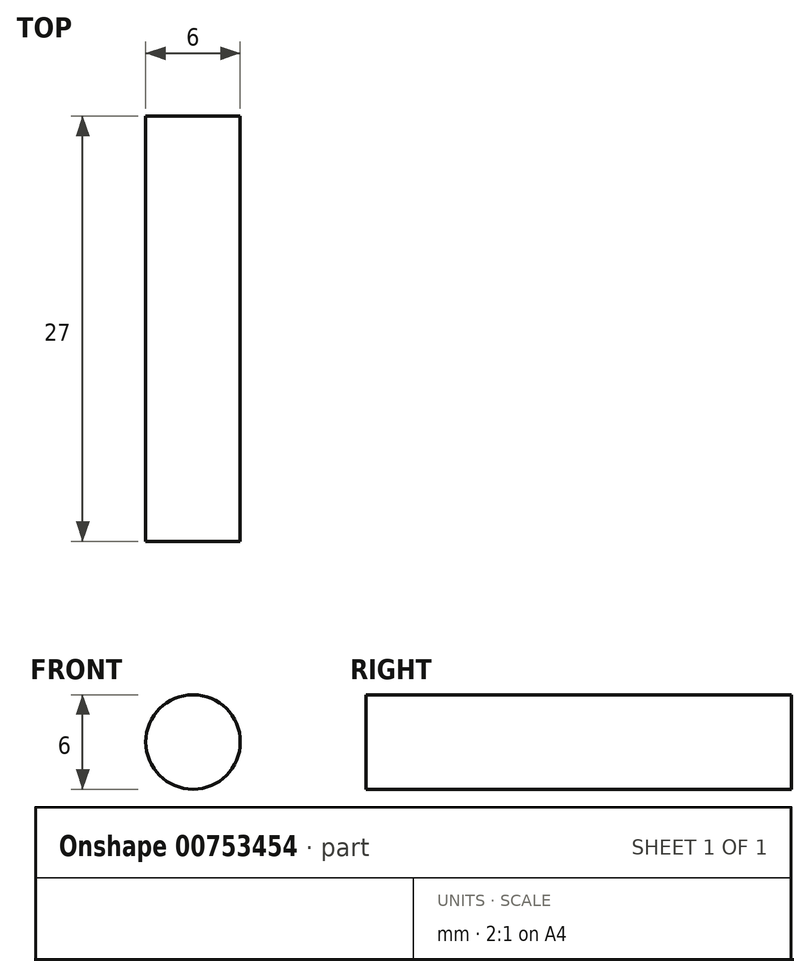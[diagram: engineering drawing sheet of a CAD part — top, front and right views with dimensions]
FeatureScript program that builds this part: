
annotation { "Feature Type Name" : "Feature", "Feature Type Description" : "" }
export const myFeature = defineFeature(function(context is Context, id is Id, definition is map)
    precondition{}
    {
        {
            var Q0;
            Q0=qCreatedBy(makeId("Front.planeOp"),FACE);
            var sketch = newSketch(context, id + "F0", { "sketchPlane" : qUnion([Q0])});
            skCircle(sketch, "E0", {"center": v(0, 0) * mm, "radius": 3 * mm});
            skSolve(sketch);
        }
        {
            var Q0;
            Q0=makeQuery(id+"F0.imprint","IMPRINT",FACE,{"disambiguationData":[TD([[makeQuery(id+"F0.imprint","IMPRINT",EDGE,{"derivedFrom":sQuery(id+"F0.wireOp",EDGE,"E0")}),1.0]])]});
            extrude(context, id + "F1", {"entities" : qUnion([Q0]), "depth" : 27 * mm, "offsetDistance" : 25 * mm});
        }
    });
